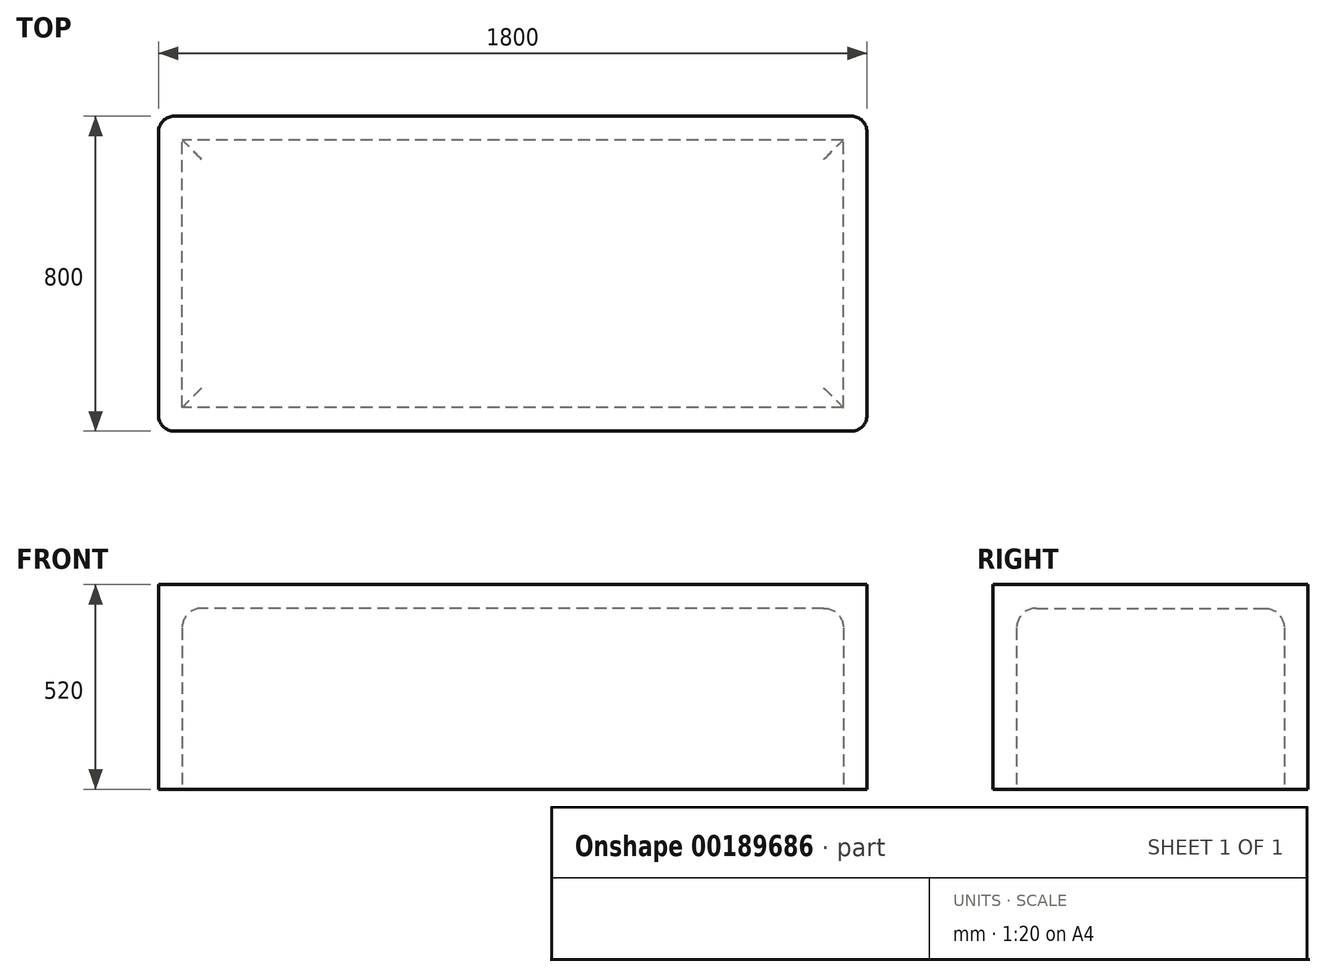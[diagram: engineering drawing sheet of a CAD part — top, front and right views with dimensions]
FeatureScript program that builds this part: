
annotation { "Feature Type Name" : "Feature", "Feature Type Description" : "" }
export const myFeature = defineFeature(function(context is Context, id is Id, definition is map)
    precondition{}
    {
        {
            var Q0;
            Q0=qCreatedBy(makeId("Top.planeOp"),FACE);
            var sketch = newSketch(context, id + "F0", { "sketchPlane" : qUnion([Q0])});
            skLineSegment(sketch, "E0.bottom", {"start": v(900, -400) * mm, "end": v(-900, -400) * mm});
            skLineSegment(sketch, "E0.top", {"start": v(900, 400) * mm, "end": v(-900, 400) * mm});
            skLineSegment(sketch, "E0.left", {"start": v(900, -400) * mm, "end": v(900, 400) * mm});
            skLineSegment(sketch, "E0.right", {"start": v(-900, -400) * mm, "end": v(-900, 400) * mm});
            skPoint(sketch, "E0.middle", {"position": v(0, 0) * mm});
            skSolve(sketch);
        }
        {
            var Q0;
            Q0=makeQuery(id+"F0.imprint","IMPRINT",FACE,{"disambiguationData":[TD([[makeQuery(id+"F0.imprint","IMPRINT",EDGE,{"derivedFrom":sQuery(id+"F0.wireOp",EDGE,"E0.bottom")}),-1.0]])]});
            extrude(context, id + "F1", {"entities" : qUnion([Q0]), "depth" : 520 * mm});
        }
        {
            var Q0;
            Q0=makeQuery(id+"F1.opExtrude","CAP_FACE",FACE,{"disambiguationData":[OSD([sQuery(id+"F0.wireOp",EDGE,"E0.bottom"),sQuery(id+"F0.wireOp",EDGE,"E0.top"),sQuery(id+"F0.wireOp",EDGE,"E0.left"),sQuery(id+"F0.wireOp",EDGE,"E0.right")])],"isStart":true});
            shell(context, id + "F2", {"entities" : qUnion([Q0]), "thickness" : 60 * mm});
        }
        {
            var Q0;
            Q0=makeQuery(id+"F2.opShell","OFFSET_FACE",FACE,{"disambiguationData":[OSD([sQuery(id+"F0.wireOp",EDGE,"E0.bottom"),sQuery(id+"F0.wireOp",EDGE,"E0.top"),sQuery(id+"F0.wireOp",EDGE,"E0.left"),sQuery(id+"F0.wireOp",EDGE,"E0.right")])]});
            fillet(context, id + "F3", {"entities" : qUnion([Q0]), "radius" : 50 * mm, "tangentPropagation" : true, "allowEdgeOverflow" : false});
        }
        {
            var Q0;
            Q0=makeQuery(id+"F1.opExtrude","SWEPT_EDGE",EDGE,{"disambiguationData":[OSD([sQuery(id+"F0.wireOp",EDGE,"E0.top"),sQuery(id+"F0.wireOp",EDGE,"E0.left")])]});
            var Q1;
            Q1=makeQuery(id+"F1.opExtrude","SWEPT_EDGE",EDGE,{"disambiguationData":[OSD([sQuery(id+"F0.wireOp",EDGE,"E0.bottom"),sQuery(id+"F0.wireOp",EDGE,"E0.left")])]});
            var Q2;
            Q2=makeQuery(id+"F1.opExtrude","SWEPT_EDGE",EDGE,{"disambiguationData":[OSD([sQuery(id+"F0.wireOp",EDGE,"E0.bottom"),sQuery(id+"F0.wireOp",EDGE,"E0.right")])]});
            var Q3;
            Q3=makeQuery(id+"F1.opExtrude","SWEPT_EDGE",EDGE,{"disambiguationData":[OSD([sQuery(id+"F0.wireOp",EDGE,"E0.top"),sQuery(id+"F0.wireOp",EDGE,"E0.right")])]});
            fillet(context, id + "F4", {"entities" : qUnion([Q0, Q1, Q2, Q3]), "radius" : 40 * mm, "tangentPropagation" : true, "allowEdgeOverflow" : false});
        }
    });
